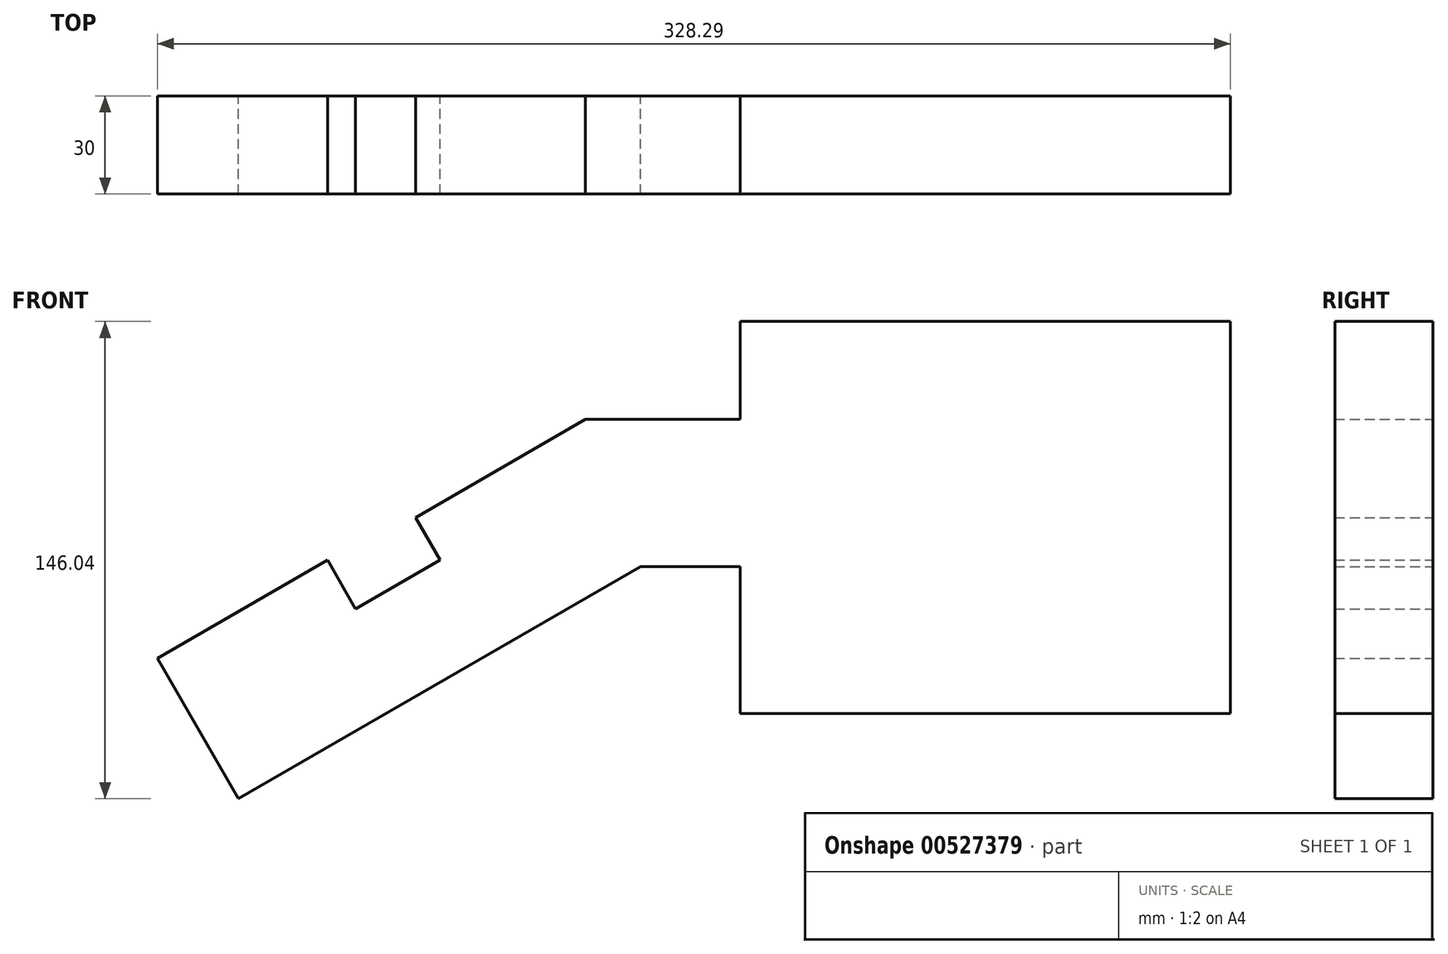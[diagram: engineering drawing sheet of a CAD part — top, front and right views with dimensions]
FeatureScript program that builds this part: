
annotation { "Feature Type Name" : "Feature", "Feature Type Description" : "" }
export const myFeature = defineFeature(function(context is Context, id is Id, definition is map)
    precondition{}
    {
        {
            var Q0;
            Q0=qCreatedBy(makeId("Front.planeOp"),FACE);
            var sketch = newSketch(context, id + "F0", { "sketchPlane" : qUnion([Q0])});
            skLineSegment(sketch, "E0", {"start": v(64.8, 42.98) * mm, "end": v(-55.2, 42.98) * mm});
            skLineSegment(sketch, "E1", {"start": v(-55.2, 42.98) * mm, "end": v(-107.15, 13) * mm});
            skLineSegment(sketch, "E2", {"start": v(-107.15, 13) * mm, "end": v(-99.65, 0) * mm});
            skLineSegment(sketch, "E3", {"start": v(-99.65, 0) * mm, "end": v(-125.56, -14.96) * mm});
            skLineSegment(sketch, "E4", {"start": v(-125.56, -14.96) * mm, "end": v(-134.17, -0.05) * mm});
            skLineSegment(sketch, "E5", {"start": v(-134.17, -0.05) * mm, "end": v(-186.2, -30.09) * mm});
            skLineSegment(sketch, "E6", {"start": v(-186.2, -30.09) * mm, "end": v(-161.4, -73.06) * mm});
            skLineSegment(sketch, "E7", {"start": v(-161.4, -73.06) * mm, "end": v(-38.35, -2.02) * mm});
            skLineSegment(sketch, "E8", {"start": v(-38.35, -2.02) * mm, "end": v(64.8, -2.02) * mm});
            skLineSegment(sketch, "E9", {"start": v(64.8, -2.02) * mm, "end": v(64.8, 42.98) * mm});
            skLineSegment(sketch, "E10", {"start": v(-7.92, -2.02) * mm, "end": v(-7.92, -47.02) * mm});
            skLineSegment(sketch, "E11", {"start": v(-7.92, -47.02) * mm, "end": v(142.08, -47.02) * mm});
            skLineSegment(sketch, "E12", {"start": v(142.08, -47.02) * mm, "end": v(142.08, 72.98) * mm});
            skLineSegment(sketch, "E13", {"start": v(142.08, 72.98) * mm, "end": v(-7.92, 72.98) * mm});
            skLineSegment(sketch, "E14", {"start": v(-7.92, 72.98) * mm, "end": v(-7.92, 42.98) * mm});
            skSolve(sketch);
        }
        {
            var Q0;
            Q0 = qSketchRegion(id + "F0", true);
            extrude(context, id + "F1", {"entities" : qUnion([Q0]), "depth" : 30 * mm, "offsetDistance" : 25 * mm});
        }
    });
